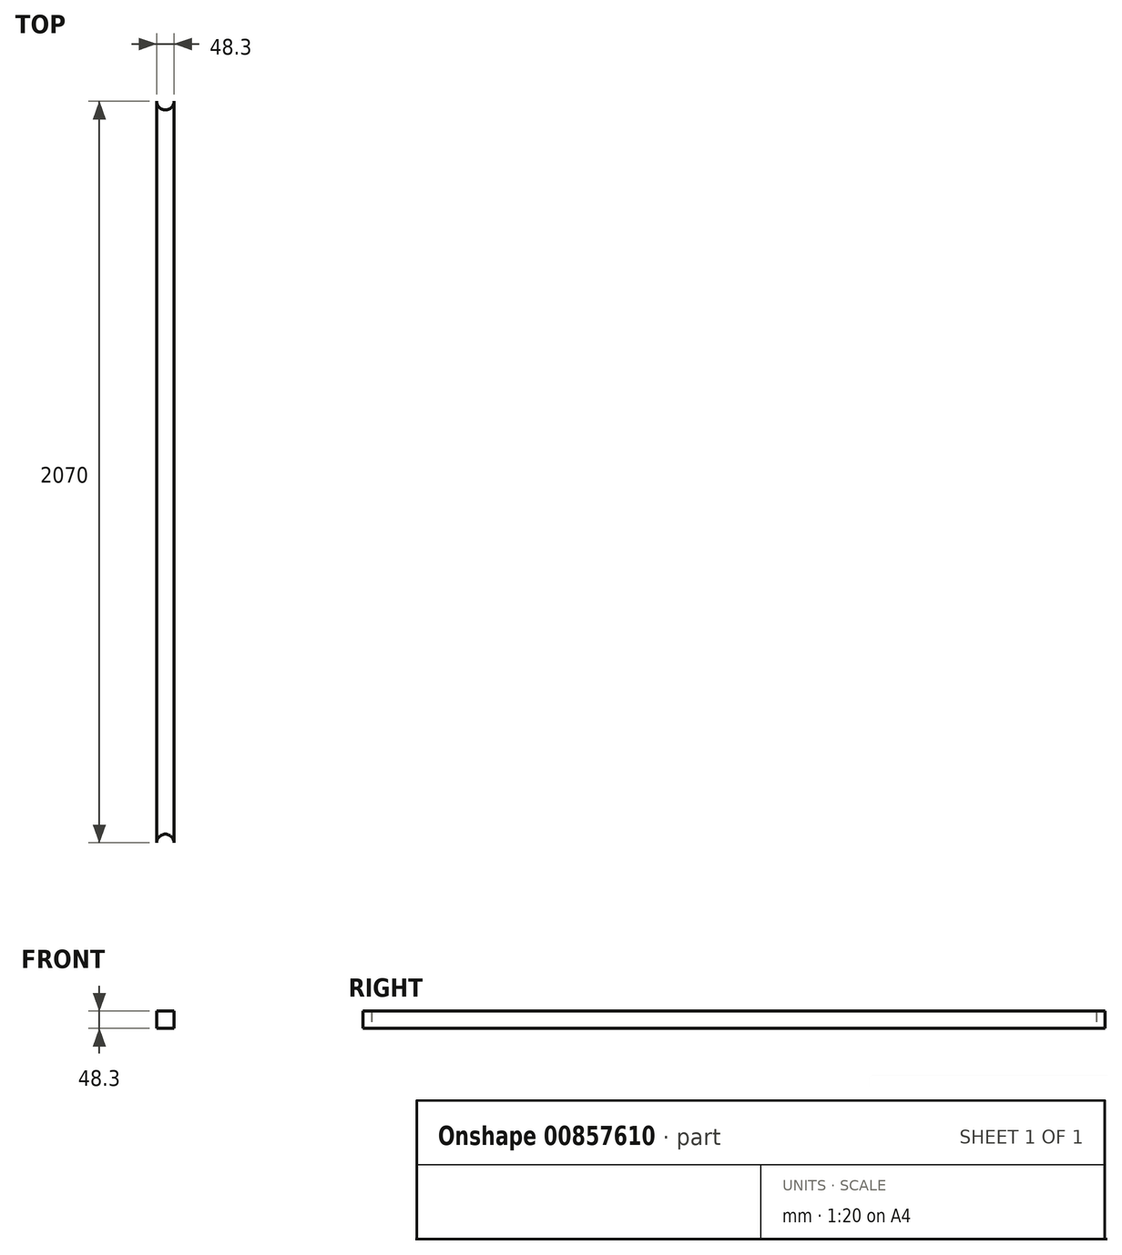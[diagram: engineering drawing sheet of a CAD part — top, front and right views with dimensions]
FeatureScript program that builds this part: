
annotation { "Feature Type Name" : "Feature", "Feature Type Description" : "" }
export const myFeature = defineFeature(function(context is Context, id is Id, definition is map)
    precondition{}
    {
        {
            var Q0;
            Q0=qCreatedBy(makeId("Top.planeOp"),FACE);
            var sketch = newSketch(context, id + "F0", { "sketchPlane" : qUnion([Q0])});
            skLineSegment(sketch, "E0.left", {"start": v(24.15, 1035) * mm, "end": v(24.15, -1035) * mm});
            skLineSegment(sketch, "E0.right", {"start": v(-24.15, 1035) * mm, "end": v(-24.15, -1035) * mm});
            skPoint(sketch, "E0.middle", {"position": v(0, 0) * mm});
            skArc(sketch, "E1", {"start": v(-24.15, 1035) * mm, "mid": v(0, 1010.85) * mm, "end": v(24.15, 1035) * mm});
            skArc(sketch, "E2", {"start": v(24.15, -1035) * mm, "mid": v(0, -1010.85) * mm, "end": v(-24.15, -1035) * mm});
            skSolve(sketch);
        }
        {
            var Q0;
            Q0 = qSketchRegion(id + "F0", true);
            extrude(context, id + "F1", {"entities" : qUnion([Q0]), "endBound" : BoundingType.SYMMETRIC, "depth" : 48.3 * mm, "offsetDistance" : 25 * mm});
        }
    });
